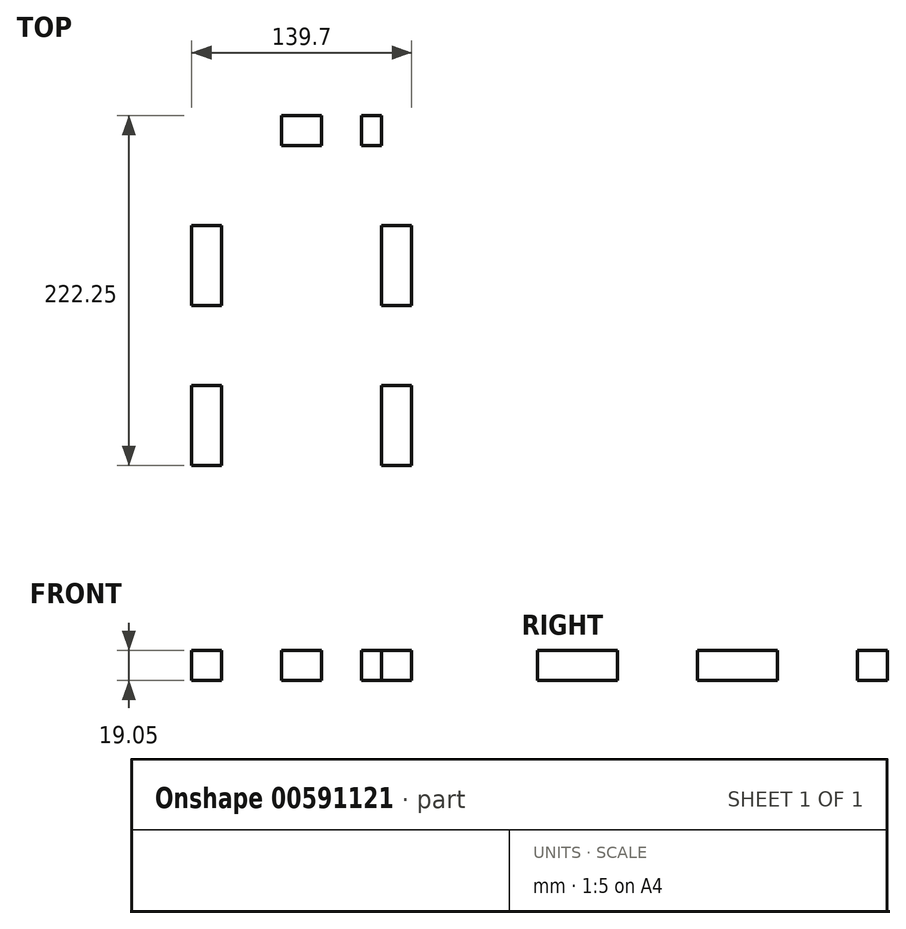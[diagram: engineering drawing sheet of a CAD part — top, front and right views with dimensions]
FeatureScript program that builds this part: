
annotation { "Feature Type Name" : "Feature", "Feature Type Description" : "" }
export const myFeature = defineFeature(function(context is Context, id is Id, definition is map)
    precondition{}
    {
        {
            var Q0;
            Q0=qCreatedBy(makeId("Top.planeOp"),FACE);
            var sketch = newSketch(context, id + "F0", { "sketchPlane" : qUnion([Q0])});
            skLineSegment(sketch, "E0.bottom", {"start": v(-101.6, 136.34) * mm, "end": v(0, 136.34) * mm});
            skLineSegment(sketch, "E0.top", {"start": v(-101.6, -117.66) * mm, "end": v(0, -117.66) * mm});
            skLineSegment(sketch, "E0.left", {"start": v(-101.6, 136.34) * mm, "end": v(-101.6, -117.66) * mm});
            skLineSegment(sketch, "E0.right", {"start": v(0, 136.34) * mm, "end": v(0, -117.66) * mm});
            skLineSegment(sketch, "E1", {"start": v(-101.6, 136.34) * mm, "end": v(-88.9, 136.34) * mm});
            skLineSegment(sketch, "E2", {"start": v(0, 136.34) * mm, "end": v(-12.7, 136.34) * mm});
            skLineSegment(sketch, "E3", {"start": v(-25.4, 136.34) * mm, "end": v(0, 136.34) * mm});
            skLineSegment(sketch, "E4", {"start": v(-101.6, -117.66) * mm, "end": v(-101.6, -66.86) * mm});
            skLineSegment(sketch, "E5", {"start": v(-101.6, 136.34) * mm, "end": v(-101.6, 85.54) * mm});
            skLineSegment(sketch, "E6", {"start": v(-101.6, -66.86) * mm, "end": v(-120.65, -66.86) * mm});
            skLineSegment(sketch, "E7", {"start": v(-120.65, -66.86) * mm, "end": v(-120.65, -16.06) * mm});
            skLineSegment(sketch, "E8", {"start": v(-120.65, -16.06) * mm, "end": v(-101.6, -16.06) * mm});
            skLineSegment(sketch, "E9", {"start": v(-101.6, -16.06) * mm, "end": v(-101.6, 34.74) * mm});
            skLineSegment(sketch, "E10", {"start": v(-101.6, 34.74) * mm, "end": v(-120.65, 34.74) * mm});
            skLineSegment(sketch, "E11", {"start": v(-120.65, 34.74) * mm, "end": v(-120.65, 85.54) * mm});
            skLineSegment(sketch, "E12", {"start": v(-120.65, 85.54) * mm, "end": v(-101.6, 85.54) * mm});
            skLineSegment(sketch, "E13", {"start": v(-101.6, 208.75) * mm, "end": v(0, 208.75) * mm});
            skLineSegment(sketch, "E14", {"start": v(0, 208.75) * mm, "end": v(0, -112.42) * mm, "construction": true});
            skLineSegment(sketch, "E15.MirrorCS", {"start": v(120.65, 85.54) * mm, "end": v(101.6, 85.54) * mm});
            skLineSegment(sketch, "E16.MirrorCS", {"start": v(120.65, 34.74) * mm, "end": v(120.65, 85.54) * mm});
            skLineSegment(sketch, "E17.MirrorCS", {"start": v(101.6, 34.74) * mm, "end": v(120.65, 34.74) * mm});
            skLineSegment(sketch, "E18.MirrorCS", {"start": v(120.65, -16.06) * mm, "end": v(101.6, -16.06) * mm});
            skLineSegment(sketch, "E19.MirrorCS", {"start": v(120.65, -66.86) * mm, "end": v(120.65, -16.06) * mm});
            skLineSegment(sketch, "E20.MirrorCS", {"start": v(101.6, -66.86) * mm, "end": v(120.65, -66.86) * mm});
            skLineSegment(sketch, "E21", {"start": v(-101.6, 9.34) * mm, "end": v(89.85, 9.34) * mm, "construction": true});
            skLineSegment(sketch, "E22.MirrorCS", {"start": v(0, -117.66) * mm, "end": v(0, -101.22) * mm});
            skLineSegment(sketch, "E23.MirrorCS", {"start": v(22.02, -101.22) * mm, "end": v(47.42, -101.22) * mm});
            skLineSegment(sketch, "E24", {"start": v(-50.8, -117.66) * mm, "end": v(-50.8, 136.34) * mm, "construction": true});
            skLineSegment(sketch, "E25", {"start": v(0, -66.86) * mm, "end": v(19.05, -66.86) * mm});
            skLineSegment(sketch, "E26", {"start": v(19.05, -66.86) * mm, "end": v(19.05, -16.06) * mm});
            skLineSegment(sketch, "E27", {"start": v(19.05, -16.06) * mm, "end": v(0, -16.06) * mm});
            skLineSegment(sketch, "E28", {"start": v(0, 34.74) * mm, "end": v(19.05, 34.74) * mm});
            skLineSegment(sketch, "E29", {"start": v(19.05, 34.74) * mm, "end": v(19.05, 85.54) * mm});
            skLineSegment(sketch, "E30", {"start": v(19.05, 85.54) * mm, "end": v(0, 85.54) * mm});
            skLineSegment(sketch, "E31", {"start": v(-101.6, 159.72) * mm, "end": v(-88.9, 159.72) * mm, "construction": true});
            skLineSegment(sketch, "E32", {"start": v(-88.9, 159.72) * mm, "end": v(-63.5, 159.72) * mm, "construction": true});
            skLineSegment(sketch, "E33", {"start": v(-63.5, 159.72) * mm, "end": v(-38.1, 159.72) * mm, "construction": true});
            skLineSegment(sketch, "E34", {"start": v(-38.1, 159.72) * mm, "end": v(-12.7, 159.72) * mm, "construction": true});
            skLineSegment(sketch, "E35", {"start": v(-12.7, 159.72) * mm, "end": v(0, 159.72) * mm, "construction": true});
            skLineSegment(sketch, "E36", {"start": v(-88.9, 136.34) * mm, "end": v(-88.9, 155.39) * mm});
            skLineSegment(sketch, "E37", {"start": v(-63.5, 155.39) * mm, "end": v(-63.5, 136.34) * mm});
            skLineSegment(sketch, "E38", {"start": v(-38.1, 136.34) * mm, "end": v(-38.1, 155.39) * mm});
            skLineSegment(sketch, "E39", {"start": v(-12.7, 155.39) * mm, "end": v(-12.7, 136.34) * mm});
            skLineSegment(sketch, "E40", {"start": v(-12.7, 155.39) * mm, "end": v(0, 155.39) * mm, "construction": true});
            skLineSegment(sketch, "E41", {"start": v(-38.1, 155.39) * mm, "end": v(-63.5, 155.39) * mm, "construction": true});
            skLineSegment(sketch, "E42", {"start": v(-88.9, 155.39) * mm, "end": v(-101.6, 155.39) * mm, "construction": true});
            skLineSegment(sketch, "E43", {"start": v(0, 155.39) * mm, "end": v(0, 136.34) * mm});
            skLineSegment(sketch, "E44", {"start": v(0, 155.39) * mm, "end": v(-12.7, 155.39) * mm});
            skLineSegment(sketch, "E45", {"start": v(-38.1, 155.39) * mm, "end": v(-63.5, 155.39) * mm});
            skLineSegment(sketch, "E46", {"start": v(-88.9, 155.39) * mm, "end": v(-101.6, 155.39) * mm});
            skLineSegment(sketch, "E47", {"start": v(-101.6, 136.34) * mm, "end": v(-101.6, 155.39) * mm});
            skSolve(sketch);
        }
        {
            var Q0;
            {var subQ2=sQuery(id+"F0.wireOp",EDGE,"E10");Q0=makeQuery(id+"F0.imprint","IMPRINT",FACE,{"disambiguationData":[TD([[makeQuery(id+"F0.imprint","IMPRINT",EDGE,{"derivedFrom":subQ2}),-1.0]])]});}
            var Q1;
            {var subQ0=sQuery(id+"F0.wireOp",EDGE,"E6");Q1=makeQuery(id+"F0.imprint","IMPRINT",FACE,{"disambiguationData":[TD([[makeQuery(id+"F0.imprint","IMPRINT",EDGE,{"derivedFrom":subQ0}),-1.0]])]});}
            var Q2;
            {var subQ0=sQuery(id+"F0.wireOp",EDGE,"E15.MirrorCS");Q2=makeQuery(id+"F0.imprint","IMPRINT",FACE,{"disambiguationData":[TD([[makeQuery(id+"F0.imprint","IMPRINT",EDGE,{"derivedFrom":subQ0}),1.0]])]});}
            var Q3;
            {var subQ0=sQuery(id+"F0.wireOp",EDGE,"E18.MirrorCS");Q3=makeQuery(id+"F0.imprint","IMPRINT",FACE,{"disambiguationData":[TD([[makeQuery(id+"F0.imprint","IMPRINT",EDGE,{"derivedFrom":subQ0}),1.0]])]});}
            var Q4;
            {var subQ5=sQuery(id+"F0.wireOp",EDGE,"E1");Q4=makeQuery(id+"F0.imprint","IMPRINT",FACE,{"disambiguationData":[TD([[makeQuery(id+"F0.imprint","IMPRINT",EDGE,{"derivedFrom":subQ5}),-1.0]])]});}
            var Q5;
            {var subQ0=sQuery(id+"F0.wireOp",EDGE,"E25");Q5=makeQuery(id+"F0.imprint","IMPRINT",FACE,{"disambiguationData":[TD([[makeQuery(id+"F0.imprint","IMPRINT",EDGE,{"derivedFrom":subQ0}),1.0]])]});}
            var Q6;
            {var subQ0=sQuery(id+"F0.wireOp",EDGE,"E28");Q6=makeQuery(id+"F0.imprint","IMPRINT",FACE,{"disambiguationData":[TD([[makeQuery(id+"F0.imprint","IMPRINT",EDGE,{"derivedFrom":subQ0}),1.0]])]});}
            var Q7;
            {var subQ4=sQuery(id+"F0.wireOp",EDGE,"E38");Q7=makeQuery(id+"F0.imprint","IMPRINT",FACE,{"disambiguationData":[TD([[makeQuery(id+"F0.imprint","IMPRINT",EDGE,{"derivedFrom":subQ4}),-1.0]])]});}
            var Q8;
            {var subQ0=sQuery(id+"F0.wireOp",EDGE,"E36");Q8=makeQuery(id+"F0.imprint","IMPRINT",FACE,{"disambiguationData":[TD([[makeQuery(id+"F0.imprint","IMPRINT",EDGE,{"derivedFrom":subQ0}),-1.0]])]});}
            var Q9;
            {var subQ0=sQuery(id+"F0.wireOp",EDGE,"E43");Q9=makeQuery(id+"F0.imprint","IMPRINT",FACE,{"disambiguationData":[TD([[makeQuery(id+"F0.imprint","IMPRINT",EDGE,{"derivedFrom":subQ0}),-1.0]])]});}
            var Q10;
            {var subQ0=sQuery(id+"F0.wireOp",EDGE,"E37");Q10=makeQuery(id+"F0.imprint","IMPRINT",FACE,{"disambiguationData":[TD([[makeQuery(id+"F0.imprint","IMPRINT",EDGE,{"derivedFrom":subQ0}),1.0]])]});}
            var Q11;
            Q11=makeQuery(id+"F0.imprint","IMPRINT",FACE,{"disambiguationData":[TD([[makeQuery(id+"F0.imprint","IMPRINT",EDGE,{"derivedFrom":sQuery(id+"F0.wireOp",EDGE,"E1")}),1.0]])]});
            extrude(context, id + "F1", {"entities" : qUnion([Q0, Q1, Q2, Q3, Q4, Q5, Q6, Q7, Q8, Q9, Q10, Q11]), "depth" : 19.05 * mm, "offsetDistance" : 25.4 * mm});
        }
    });
